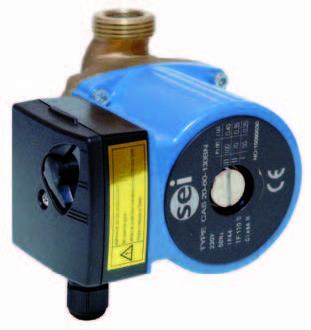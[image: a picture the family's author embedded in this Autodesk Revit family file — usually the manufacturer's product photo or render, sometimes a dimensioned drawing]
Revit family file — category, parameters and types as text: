
# Revit family: CAS_20-40BN-AC52150
name_source: partatom
category: Aparatos eléctricos
revit_build: Autodesk Revit 2016 (Build: 20150220_1215(x64)
units: mm (PartAtom-declared; Revit-internal decimal feet)

## family parameters
Compartido = No
Corte con vacíos al cargar = No
Cota de conector redondo = Diámetro de uso
Mantener orientación de anotación = No
Número OmniClass = 23.80.00.00
Punto de cálculo de habitación = No
Se basa en plano de trabajo = No
Siempre vertical = Sí
Tipo de pieza = Caja de conexiones
Título OmniClass = Electric Power and Lighting

## types (2) — shared parameters
Fabricante = SALVADOR ESCODA
URL = www.salvadorescoda.com
zero-valued in all types: Costo

## per-type parameters (varying)
| type | Aislamiento | Caudal | Conexión racores | Código de montaje | Descripción | Dimensiones Unidad Interior | Imagen de tipo | Intensidad máx. | Modelo | Motor | Máx. presión trabajo | Peso | Potencia máx | Presión disponible | Protección | Rango temperatura agua | Regulable | Temperatura ambiente |
| MVD-22T2 | 35 dB(A) |  |  | CL23370 | CONDUCTO BAJA SILUETA | 700 x 210 x 500 mm | <Ninguno> |  | MVD-22T2/DHN1-DA5 | 521 m3/h | 2,2kW / 39W | 17,5 kg neto |  |  | 6,35 mm (1/4") | 2,6kW / 39W |  | DC / WZDK100-38GS |
| CAS | Clase H | 1 m3/h | 1" DN | AC52150 | BOMBA CIRCULADORA PARA ACS | 130 x 130 x 130 mm | SEI_CAS.jpg | 0,28 A | CAS 20-40 BN | 2 polos, 1x230V - 50Hz | 10 bar | 2,9 Kgs | 65 W | 3 m.c.a. | IP 44 | 2º a 110 ºC | 3 velocidades | Hasta 40ºC |
